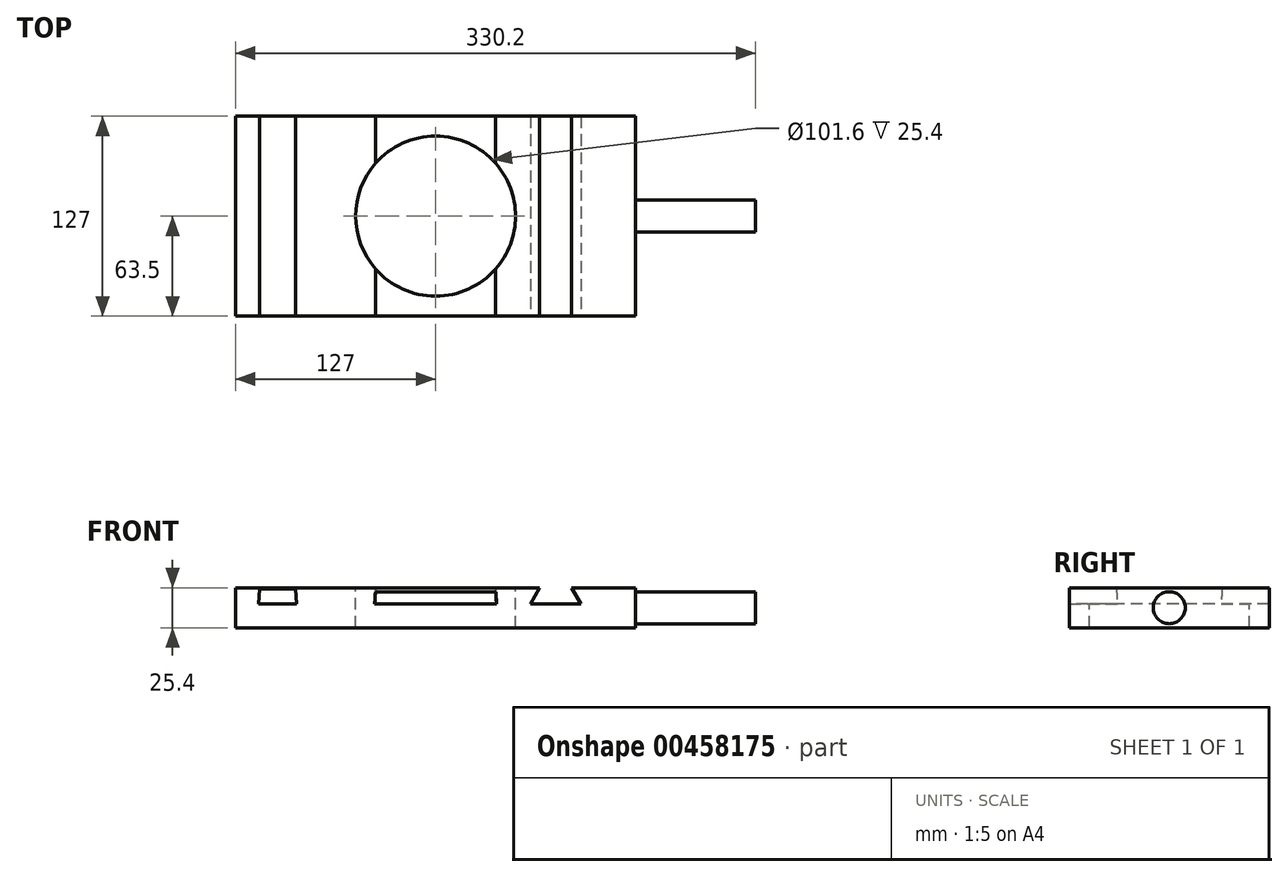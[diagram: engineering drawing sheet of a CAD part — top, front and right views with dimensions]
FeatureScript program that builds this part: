
annotation { "Feature Type Name" : "Feature", "Feature Type Description" : "" }
export const myFeature = defineFeature(function(context is Context, id is Id, definition is map)
    precondition{}
    {
        {
            var Q0;
            Q0=qCreatedBy(makeId("Top.planeOp"),FACE);
            var sketch = newSketch(context, id + "F0", { "sketchPlane" : qUnion([Q0])});
            skLineSegment(sketch, "E0.bottom", {"start": v(-127, 63.5) * mm, "end": v(127, 63.5) * mm});
            skLineSegment(sketch, "E0.top", {"start": v(-127, -63.5) * mm, "end": v(127, -63.5) * mm});
            skLineSegment(sketch, "E0.left", {"start": v(-127, 63.5) * mm, "end": v(-127, -63.5) * mm});
            skLineSegment(sketch, "E0.right", {"start": v(127, 63.5) * mm, "end": v(127, -63.5) * mm});
            skPoint(sketch, "E0.middle", {"position": v(0, 0) * mm});
            skSolve(sketch);
        }
        {
            var Q0;
            Q0=makeQuery(id+"F0.imprint","IMPRINT",FACE,{"disambiguationData":[TD([[makeQuery(id+"F0.imprint","IMPRINT",EDGE,{"derivedFrom":sQuery(id+"F0.wireOp",EDGE,"E0.bottom")}),-1.0]])]});
            var sketch = newSketch(context, id + "F1", { "sketchPlane" : qUnion([Q0])});
            skCircle(sketch, "E1", {"center": v(0, 0) * mm, "radius": 50.8 * mm});
            skSolve(sketch);
        }
        {
            var Q0;
            Q0=makeQuery(id+"F1.imprint","IMPRINT",FACE,{"disambiguationData":[TD([[makeQuery(id+"F1.imprint","IMPRINT",EDGE,{"derivedFrom":sQuery(id+"F1.wireOp",EDGE,"E1")}),-1.0]])]});
            extrude(context, id + "F2", {"entities" : qUnion([Q0]), "oppositeDirection" : true, "depth" : 25.4 * mm});
        }
        {
            var Q0;
            Q0=makeQuery(id+"F0.imprint","IMPRINT",FACE,{"disambiguationData":[TD([[makeQuery(id+"F0.imprint","IMPRINT",EDGE,{"derivedFrom":sQuery(id+"F0.wireOp",EDGE,"E0.bottom")}),-1.0]])]});
            var sketch = newSketch(context, id + "F3", { "sketchPlane" : qUnion([Q0])});
            skLineSegment(sketch, "E2.bottom", {"start": v(-111.76, 63.5) * mm, "end": v(-88.82, 63.5) * mm});
            skLineSegment(sketch, "E2.top", {"start": v(-111.76, -63.47) * mm, "end": v(-88.82, -63.47) * mm});
            skLineSegment(sketch, "E2.left", {"start": v(-111.76, 63.5) * mm, "end": v(-111.76, -63.47) * mm});
            skLineSegment(sketch, "E2.right", {"start": v(-88.82, 63.5) * mm, "end": v(-88.82, -63.47) * mm});
            skLineSegment(sketch, "E3", {"start": v(-38.1, 63.5) * mm, "end": v(-38.1, -63.36) * mm});
            skPoint(sketch, "E3.startSnap0", {"position": v(-100.3, 63.5) * mm});
            skLineSegment(sketch, "E4", {"start": v(-38.1, -63.36) * mm, "end": v(38.1, -63.36) * mm});
            skLineSegment(sketch, "E5", {"start": v(38.1, -63.36) * mm, "end": v(38.1, 63.5) * mm});
            skLineSegment(sketch, "E6", {"start": v(-38.1, 63.5) * mm, "end": v(38.1, 63.5) * mm});
            skPoint(sketch, "E7", {"position": v(0, 0) * mm});
            skLineSegment(sketch, "E8", {"start": v(0, 63.5) * mm, "end": v(0, -63.36) * mm, "construction": true});
            skSolve(sketch);
        }
        {
            var Q0;
            Q0=makeQuery(id+"F2.opExtrude","SWEPT_FACE",FACE,{"disambiguationData":[OSD([sQuery(id+"F0.wireOp",EDGE,"E0.top")])]});
            var sketch = newSketch(context, id + "F4", { "sketchPlane" : qUnion([Q0])});
            skLineSegment(sketch, "E9", {"start": v(66.04, 0) * mm, "end": v(60.17, -10.16) * mm});
            skLineSegment(sketch, "E10", {"start": v(60.17, -10.16) * mm, "end": v(92.23, -10.16) * mm});
            skLineSegment(sketch, "E11", {"start": v(92.23, -10.16) * mm, "end": v(86.36, 0) * mm});
            skLineSegment(sketch, "E12", {"start": v(86.36, 0) * mm, "end": v(66.04, 0) * mm});
            skLineSegment(sketch, "E13", {"start": v(76.2, -10.16) * mm, "end": v(76.2, 0) * mm, "construction": true});
            skSolve(sketch);
        }
        {
            var Q0;
            Q0=makeQuery(id+"F4.imprint","IMPRINT",FACE,{"disambiguationData":[TD([[makeQuery(id+"F4.imprint","IMPRINT",EDGE,{"derivedFrom":sQuery(id+"F4.wireOp",EDGE,"E9")}),1.0]])]});
            extrude(context, id + "F5", {"entities" : qUnion([Q0]), "operationType" : NewBodyOperationType.REMOVE, "endBound" : BoundingType.THROUGH_ALL, "oppositeDirection" : true, "depth" : 25.4 * mm});
        }
        {
            var Q0;
            Q0=makeQuery(id+"F2.opExtrude","SWEPT_FACE",FACE,{"disambiguationData":[OSD([sQuery(id+"F0.wireOp",EDGE,"E0.right")])]});
            var sketch = newSketch(context, id + "F6", { "sketchPlane" : qUnion([Q0])});
            skCircle(sketch, "E14", {"center": v(0, -12.7) * mm, "radius": 10.16 * mm});
            skPoint(sketch, "E14.centerSnap0", {"position": v(-63.5, -12.7) * mm});
            skSolve(sketch);
        }
        {
            var Q0;
            {var subQ0=sQuery(id+"F3.wireOp",EDGE,"E2.top");Q0=makeQuery(id+"F3.imprint","IMPRINT",FACE,{"disambiguationData":[TD([[makeQuery(id+"F3.imprint","IMPRINT",EDGE,{"derivedFrom":subQ0}),1.0]])]});}
            var Q1;
            {var subQ0=sQuery(id+"F3.wireOp",EDGE,"E4");Q1=makeQuery(id+"F3.imprint","IMPRINT",FACE,{"disambiguationData":[TD([[makeQuery(id+"F3.imprint","IMPRINT",EDGE,{"derivedFrom":subQ0}),1.0]])]});}
            extrude(context, id + "F7", {"entities" : qUnion([Q0, Q1]), "operationType" : NewBodyOperationType.REMOVE, "oppositeDirection" : true, "depth" : 10.4 * mm, "hasDraft" : true, "draftAngle" : 3 * degree});
        }
        {
            var Q0;
            Q0=makeQuery(id+"F6.imprint","IMPRINT",FACE,{"disambiguationData":[TD([[makeQuery(id+"F6.imprint","IMPRINT",EDGE,{"derivedFrom":sQuery(id+"F6.wireOp",EDGE,"E14")}),1.0]])]});
            extrude(context, id + "F8", {"entities" : qUnion([Q0]), "operationType" : NewBodyOperationType.ADD, "depth" : 76.2 * mm});
        }
    });
